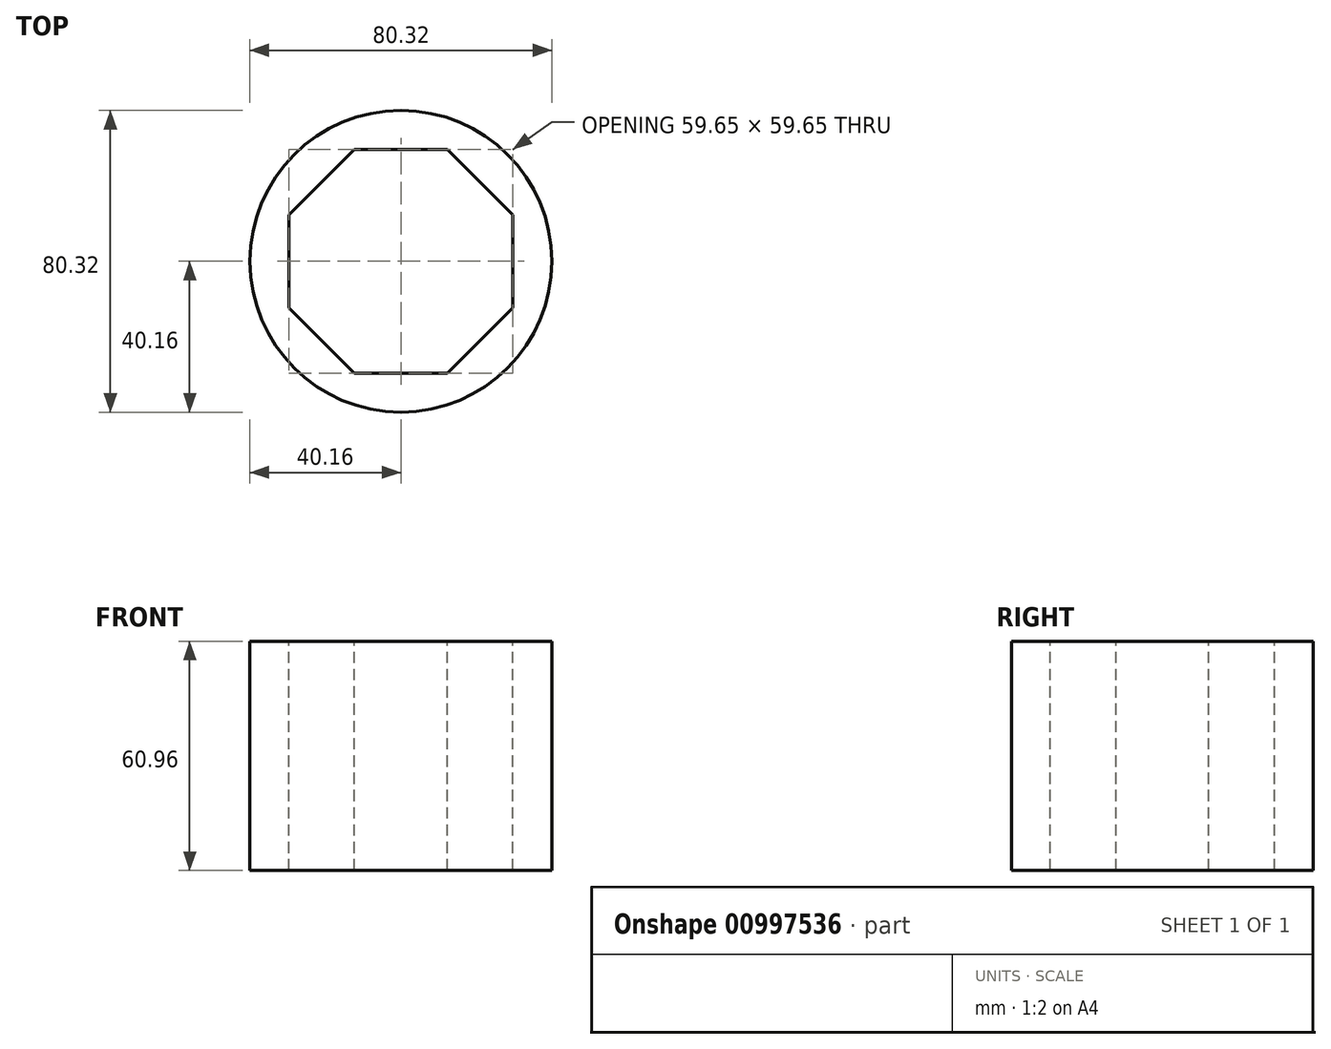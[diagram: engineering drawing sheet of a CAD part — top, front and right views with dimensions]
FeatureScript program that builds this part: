
annotation { "Feature Type Name" : "Feature", "Feature Type Description" : "" }
export const myFeature = defineFeature(function(context is Context, id is Id, definition is map)
    precondition{}
    {
        {
            var Q0;
            Q0=qCreatedBy(makeId("Top.planeOp"),FACE);
            var sketch = newSketch(context, id + "F0", { "sketchPlane" : qUnion([Q0])});
            skCircle(sketch, "E0", {"center": v(0, 0) * mm, "radius": 40.16 * mm});
            skSolve(sketch);
        }
        {
            var Q0;
            Q0=makeQuery(id+"F0.imprint","IMPRINT",FACE,{"disambiguationData":[TD([[makeQuery(id+"F0.imprint","IMPRINT",EDGE,{"derivedFrom":sQuery(id+"F0.wireOp",EDGE,"E0")}),1.0]])]});
            extrude(context, id + "F1", {"entities" : qUnion([Q0]), "depth" : 60.96 * mm, "offsetDistance" : 25.4 * mm});
        }
        {
            var Q0;
            Q0=makeQuery(id+"F1.opExtrude","CAP_FACE",FACE,{"disambiguationData":[OSD([sQuery(id+"F0.wireOp",EDGE,"E0")])],"isStart":false});
            var sketch = newSketch(context, id + "F2", { "sketchPlane" : qUnion([Q0])});
            skCircle(sketch, "E1.cCircle", {"center": v(0, 0) * mm, "radius": 29.83 * mm, "construction": true});
            skLineSegment(sketch, "E1.0", {"start": v(12.35, -29.83) * mm, "end": v(-12.35, -29.83) * mm});
            skLineSegment(sketch, "E1.1", {"start": v(-12.35, -29.83) * mm, "end": v(-29.83, -12.35) * mm});
            skLineSegment(sketch, "E1.2", {"start": v(-29.83, -12.35) * mm, "end": v(-29.83, 12.35) * mm});
            skLineSegment(sketch, "E1.3", {"start": v(-29.83, 12.35) * mm, "end": v(-12.35, 29.83) * mm});
            skLineSegment(sketch, "E1.4", {"start": v(-12.35, 29.83) * mm, "end": v(12.35, 29.83) * mm});
            skLineSegment(sketch, "E1.5", {"start": v(12.35, 29.83) * mm, "end": v(29.83, 12.35) * mm});
            skLineSegment(sketch, "E1.6", {"start": v(29.83, 12.35) * mm, "end": v(29.83, -12.35) * mm});
            skLineSegment(sketch, "E1.7", {"start": v(29.83, -12.35) * mm, "end": v(12.35, -29.83) * mm});
            skPoint(sketch, "E1.0.midPoint", {"position": v(0, -29.83) * mm});
            skSolve(sketch);
        }
        {
            var Q0;
            Q0=makeQuery(id+"F2.imprint","IMPRINT",FACE,{"disambiguationData":[TD([[makeQuery(id+"F2.imprint","IMPRINT",EDGE,{"derivedFrom":sQuery(id+"F2.wireOp",EDGE,"E1.0")}),-1.0]])]});
            extrude(context, id + "F3", {"entities" : qUnion([Q0]), "operationType" : NewBodyOperationType.REMOVE, "oppositeDirection" : true, "depth" : 183.9 * mm, "offsetDistance" : 25.4 * mm});
        }
    });
